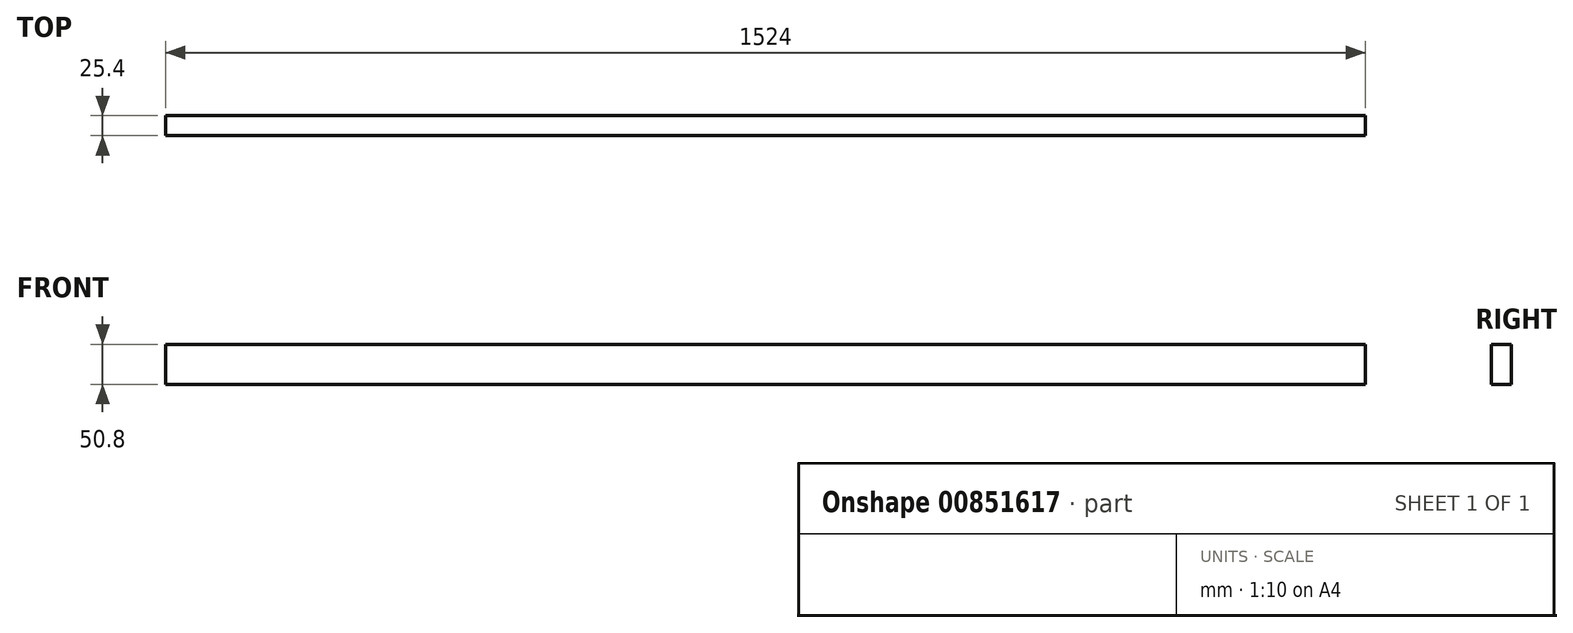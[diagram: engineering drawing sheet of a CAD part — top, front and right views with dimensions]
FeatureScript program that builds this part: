
annotation { "Feature Type Name" : "Feature", "Feature Type Description" : "" }
export const myFeature = defineFeature(function(context is Context, id is Id, definition is map)
    precondition{}
    {
        {
            var Q0;
            Q0=qCreatedBy(makeId("Front.planeOp"),FACE);
            var sketch = newSketch(context, id + "F0", { "sketchPlane" : qUnion([Q0])});
            skLineSegment(sketch, "E0", {"start": v(-351.05, 0) * mm, "end": v(-351.05, -50.8) * mm});
            skLineSegment(sketch, "E1", {"start": v(-351.05, -50.8) * mm, "end": v(1172.95, -50.8) * mm});
            skLineSegment(sketch, "E2", {"start": v(-351.05, 0) * mm, "end": v(1172.95, 0) * mm});
            skLineSegment(sketch, "E3", {"start": v(1172.95, 0) * mm, "end": v(1172.95, -50.8) * mm});
            skSolve(sketch);
        }
        {
            var Q0;
            Q0 = qSketchRegion(id + "F0", true);
            extrude(context, id + "F1", {"entities" : qUnion([Q0]), "depth" : 25.4 * mm, "offsetDistance" : 25.4 * mm});
        }
    });
